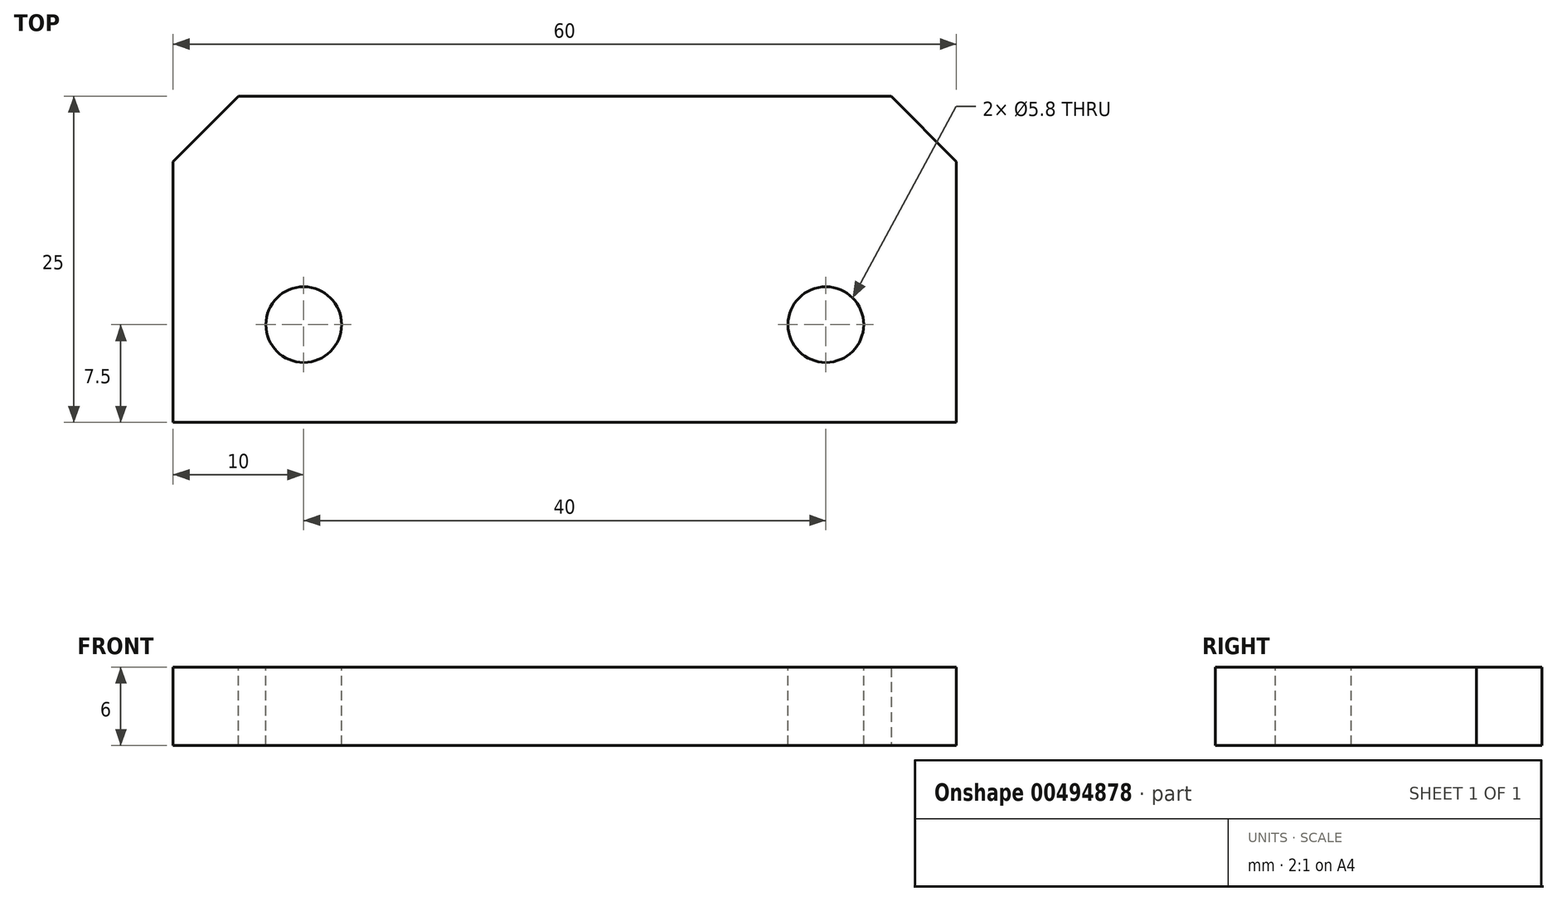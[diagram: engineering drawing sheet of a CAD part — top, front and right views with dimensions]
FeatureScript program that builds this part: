
annotation { "Feature Type Name" : "Feature", "Feature Type Description" : "" }
export const myFeature = defineFeature(function(context is Context, id is Id, definition is map)
    precondition{}
    {
        {
            var Q0;
            Q0=qCreatedBy(makeId("Top.planeOp"),FACE);
            var sketch = newSketch(context, id + "F0", { "sketchPlane" : qUnion([Q0])});
            skLineSegment(sketch, "E0.bottom", {"start": v(0, 0) * mm, "end": v(60, 0) * mm});
            skLineSegment(sketch, "E0.top", {"start": v(0, 25) * mm, "end": v(60, 25) * mm});
            skLineSegment(sketch, "E0.left", {"start": v(0, 0) * mm, "end": v(0, 25) * mm});
            skLineSegment(sketch, "E0.right", {"start": v(60, 0) * mm, "end": v(60, 25) * mm});
            skSolve(sketch);
        }
        {
            var Q0;
            Q0=qSketchRegion(id+"F0",true);
            extrude(context, id + "F1", {"entities" : qUnion([Q0]), "depth" : 6 * mm});
        }
        {
            var Q0;
            Q0=makeQuery(id+"F1.opExtrude","CAP_FACE",FACE,{"disambiguationData":[OSD([sQuery(id+"F0.wireOp",EDGE,"E0.bottom"),sQuery(id+"F0.wireOp",EDGE,"E0.top"),sQuery(id+"F0.wireOp",EDGE,"E0.left"),sQuery(id+"F0.wireOp",EDGE,"E0.right")])],"isStart":false});
            var sketch = newSketch(context, id + "F2", { "sketchPlane" : qUnion([Q0])});
            skPoint(sketch, "E1", {"position": v(10, 7.5) * mm});
            skPoint(sketch, "E2", {"position": v(50, 7.5) * mm});
            skSolve(sketch);
        }
        {
            var Q0;
            Q0=sQuery(id+"F2.wireOp",VERTEX,"E2");
            var Q1;
            Q1=sQuery(id+"F2.wireOp",VERTEX,"E1");
            var Q2;
            Q2=makeQuery(id+"F1.opExtrude","SWEPT_BODY",BODY,{"disambiguationData":[OSD([sQuery(id+"F0.wireOp",EDGE,"E0.bottom"),sQuery(id+"F0.wireOp",EDGE,"E0.top"),sQuery(id+"F0.wireOp",EDGE,"E0.left"),sQuery(id+"F0.wireOp",EDGE,"E0.right")])]});
            hole(context, id + "F3", {"style" : HoleStyle.SIMPLE, "endStyle" : HoleEndStyle.THROUGH, "standardTappedOrClearance" : lookupTablePath({ "standard" : "ISO", "size" : "5.8", "type" : "Drilled" }), "standardBlindInLast" : lookupTablePath({ "standard" : "ISO", "size" : "5.8", "type" : "Drilled" }), "holeDiameter" : 5.8 * mm, "isTappedThrough" : true, "tappedDepth" : 12.25 * mm, "tapClearance" : 3, "locations" : qUnion([Q0, Q1]), "scope" : qUnion([Q2])});
        }
        {
            var Q0;
            Q0=makeQuery(id+"F1.opExtrude","SWEPT_EDGE",EDGE,{"disambiguationData":[OSD([sQuery(id+"F0.wireOp",EDGE,"E0.top"),sQuery(id+"F0.wireOp",EDGE,"E0.right")])]});
            var Q1;
            Q1=makeQuery(id+"F1.opExtrude","SWEPT_EDGE",EDGE,{"disambiguationData":[OSD([sQuery(id+"F0.wireOp",EDGE,"E0.top"),sQuery(id+"F0.wireOp",EDGE,"E0.left")])]});
            chamfer(context, id + "F4", {"entities" : qUnion([Q0, Q1]), "width" : 5 * mm, "tangentPropagation" : true});
        }
    });
